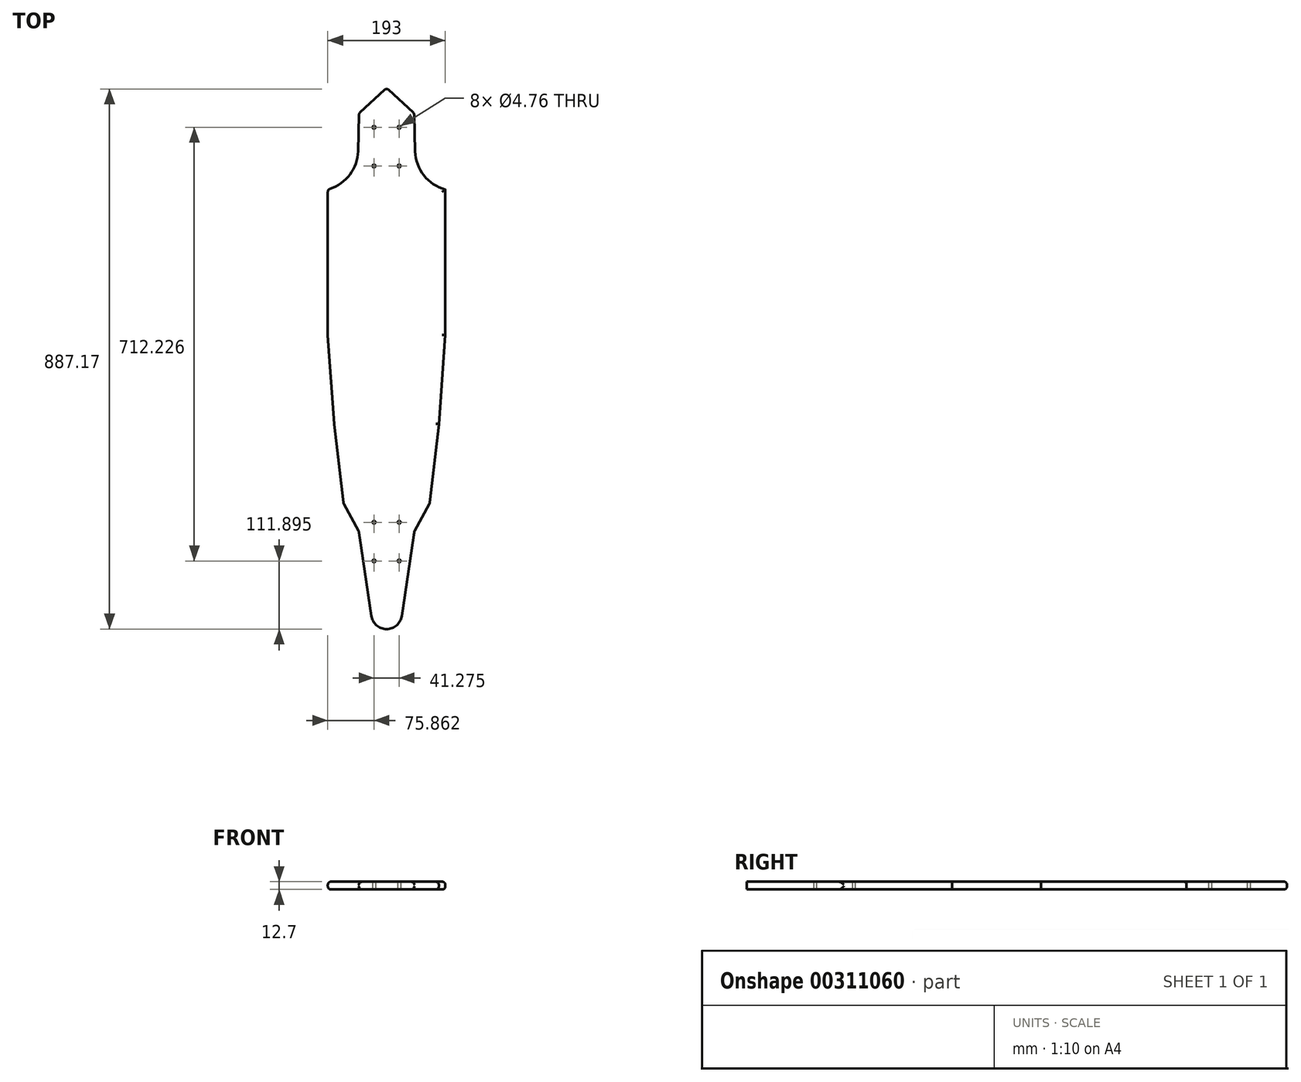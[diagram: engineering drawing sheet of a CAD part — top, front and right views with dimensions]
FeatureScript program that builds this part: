
annotation { "Feature Type Name" : "Feature", "Feature Type Description" : "" }
export const myFeature = defineFeature(function(context is Context, id is Id, definition is map)
    precondition{}
    {
        {
            var Q0;
            Q0=qCreatedBy(makeId("Top.planeOp"),FACE);
            var sketch = newSketch(context, id + "F0", { "sketchPlane" : qUnion([Q0])});
            skArc(sketch, "E0", {"start": v(-25.04, -541.51) * mm, "mid": v(-16.53, -556.97) * mm, "end": v(0, -563.11) * mm});
            skLineSegment(sketch, "E1", {"start": v(-45.6, -402.96) * mm, "end": v(-25.04, -541.51) * mm});
            skLineSegment(sketch, "E2", {"start": v(-70.57, -356.76) * mm, "end": v(-45.6, -402.96) * mm});
            skLineSegment(sketch, "E3", {"start": v(-96.5, 159.01) * mm, "end": v(-96.5, -80.18) * mm});
            skLineSegment(sketch, "E4", {"start": v(-96.5, -80.18) * mm, "end": v(-85.83, -226.36) * mm});
            skLineSegment(sketch, "E5", {"start": v(-85.83, -226.36) * mm, "end": v(-70.57, -356.76) * mm});
            skArc(sketch, "E6", {"start": v(-96.5, 159.01) * mm, "mid": v(-61.24, 182.07) * mm, "end": v(-46.84, 221.67) * mm});
            skLineSegment(sketch, "E7", {"start": v(-45.11, 284.25) * mm, "end": v(-46.84, 221.67) * mm});
            skLineSegment(sketch, "E8", {"start": v(0, 325.89) * mm, "end": v(-45.11, 284.25) * mm});
            skLineSegment(sketch, "E9.MirrorCS", {"start": v(0, 325.89) * mm, "end": v(45.11, 284.25) * mm});
            skLineSegment(sketch, "E10.MirrorCS", {"start": v(45.11, 284.25) * mm, "end": v(46.84, 221.67) * mm});
            skArc(sketch, "E11.MirrorCS", {"start": v(96.5, 159.01) * mm, "mid": v(61.24, 182.07) * mm, "end": v(46.84, 221.67) * mm});
            skLineSegment(sketch, "E12.MirrorCS", {"start": v(96.5, 159.01) * mm, "end": v(96.5, -80.18) * mm});
            skLineSegment(sketch, "E13.MirrorCS", {"start": v(96.5, -80.18) * mm, "end": v(85.83, -226.36) * mm});
            skLineSegment(sketch, "E14.MirrorCS", {"start": v(85.83, -226.36) * mm, "end": v(70.57, -356.76) * mm});
            skLineSegment(sketch, "E15.MirrorCS", {"start": v(70.57, -356.76) * mm, "end": v(45.6, -402.96) * mm});
            skLineSegment(sketch, "E16.MirrorCS", {"start": v(45.6, -402.96) * mm, "end": v(25.04, -541.51) * mm});
            skArc(sketch, "E17.MirrorCS", {"start": v(25.04, -541.51) * mm, "mid": v(16.53, -556.97) * mm, "end": v(0, -563.11) * mm});
            skCircle(sketch, "E18", {"center": v(-20.64, 197.51) * mm, "radius": 2.38 * mm});
            skCircle(sketch, "E19", {"center": v(-20.64, 261.01) * mm, "radius": 2.38 * mm});
            skCircle(sketch, "E20.MirrorC", {"center": v(20.64, 261.01) * mm, "radius": 2.38 * mm});
            skCircle(sketch, "E21.MirrorC", {"center": v(20.64, 197.51) * mm, "radius": 2.38 * mm});
            skCircle(sketch, "E22", {"center": v(20.64, -387.72) * mm, "radius": 2.38 * mm});
            skCircle(sketch, "E23", {"center": v(20.64, -451.22) * mm, "radius": 2.38 * mm});
            skCircle(sketch, "E24.MirrorC", {"center": v(-20.64, -387.72) * mm, "radius": 2.38 * mm});
            skCircle(sketch, "E25.MirrorC", {"center": v(-20.64, -451.22) * mm, "radius": 2.38 * mm});
            skLineSegment(sketch, "E26", {"start": v(0, 325.89) * mm, "end": v(0, -563.11) * mm, "construction": true});
            skLineSegment(sketch, "E27", {"start": v(93.7, -118.61) * mm, "end": v(-93.7, -118.61) * mm, "construction": true});
            skPoint(sketch, "E27.startSnap0", {"position": v(0, -118.61) * mm});
            skSolve(sketch);
        }
        {
            var Q0;
            Q0=makeQuery(id+"F0.imprint","IMPRINT",FACE,{"disambiguationData":[TD([[makeQuery(id+"F0.imprint","IMPRINT",EDGE,{"derivedFrom":sQuery(id+"F0.wireOp",EDGE,"E0")}),1.0]])]});
            extrude(context, id + "F1", {"entities" : qUnion([Q0]), "depth" : 12.7 * mm});
        }
        {
            var Q0;
            Q0=makeQuery(id+"F1.opExtrude","CAP_EDGE",EDGE,{"disambiguationData":[OSD([sQuery(id+"F0.wireOp",EDGE,"E14.MirrorCS")])],"isStart":false});
            var Q1;
            Q1=makeQuery(id+"F1.opExtrude","CAP_EDGE",EDGE,{"disambiguationData":[OSD([sQuery(id+"F0.wireOp",EDGE,"E14.MirrorCS")])],"isStart":true});
            var Q2;
            Q2=makeQuery(id+"F1.opExtrude","CAP_EDGE",EDGE,{"disambiguationData":[OSD([sQuery(id+"F0.wireOp",EDGE,"E13.MirrorCS")])],"isStart":true});
            var Q3;
            Q3=makeQuery(id+"F1.opExtrude","CAP_EDGE",EDGE,{"disambiguationData":[OSD([sQuery(id+"F0.wireOp",EDGE,"E12.MirrorCS")])],"isStart":true});
            var Q4;
            Q4=makeQuery(id+"F1.opExtrude","CAP_EDGE",EDGE,{"disambiguationData":[OSD([sQuery(id+"F0.wireOp",EDGE,"E12.MirrorCS")])],"isStart":false});
            var Q5;
            Q5=makeQuery(id+"F1.opExtrude","SWEPT_FACE",FACE,{"disambiguationData":[OSD([sQuery(id+"F0.wireOp",EDGE,"E15.MirrorCS")])]});
            var Q6;
            Q6=makeQuery(id+"F1.opExtrude","SWEPT_FACE",FACE,{"disambiguationData":[OSD([sQuery(id+"F0.wireOp",EDGE,"E2")])]});
            var Q7;
            Q7=makeQuery(id+"F1.opExtrude","SWEPT_FACE",FACE,{"disambiguationData":[OSD([sQuery(id+"F0.wireOp",EDGE,"E5")])]});
            var Q8;
            Q8=makeQuery(id+"F1.opExtrude","SWEPT_FACE",FACE,{"disambiguationData":[OSD([sQuery(id+"F0.wireOp",EDGE,"E4")])]});
            var Q9;
            Q9=makeQuery(id+"F1.opExtrude","SWEPT_FACE",FACE,{"disambiguationData":[OSD([sQuery(id+"F0.wireOp",EDGE,"E3")])]});
            var Q10;
            Q10=makeQuery(id+"F1.opExtrude","SWEPT_FACE",FACE,{"disambiguationData":[OSD([sQuery(id+"F0.wireOp",EDGE,"E6")])]});
            var Q11;
            Q11=makeQuery(id+"F1.opExtrude","SWEPT_FACE",FACE,{"disambiguationData":[OSD([sQuery(id+"F0.wireOp",EDGE,"E8")])]});
            var Q12;
            Q12=makeQuery(id+"F1.opExtrude","SWEPT_FACE",FACE,{"disambiguationData":[OSD([sQuery(id+"F0.wireOp",EDGE,"E9.MirrorCS")])]});
            var Q13;
            Q13=makeQuery(id+"F1.opExtrude","CAP_EDGE",EDGE,{"disambiguationData":[OSD([sQuery(id+"F0.wireOp",EDGE,"E11.MirrorCS")])],"isStart":false});
            var Q14;
            Q14=makeQuery(id+"F1.opExtrude","CAP_EDGE",EDGE,{"disambiguationData":[OSD([sQuery(id+"F0.wireOp",EDGE,"E11.MirrorCS")])],"isStart":true});
            var Q15;
            Q15=makeQuery(id+"F1.opExtrude","CAP_EDGE",EDGE,{"disambiguationData":[OSD([sQuery(id+"F0.wireOp",EDGE,"E10.MirrorCS")])],"isStart":true});
            fillet(context, id + "F2", {"entities" : qUnion([Q0, Q1, Q2, Q3, Q4, Q5, Q6, Q7, Q8, Q9, Q10, Q11, Q12, Q13, Q14, Q15]), "radius" : 5.08 * mm, "tangentPropagation" : true, "allowEdgeOverflow" : false});
        }
    });
